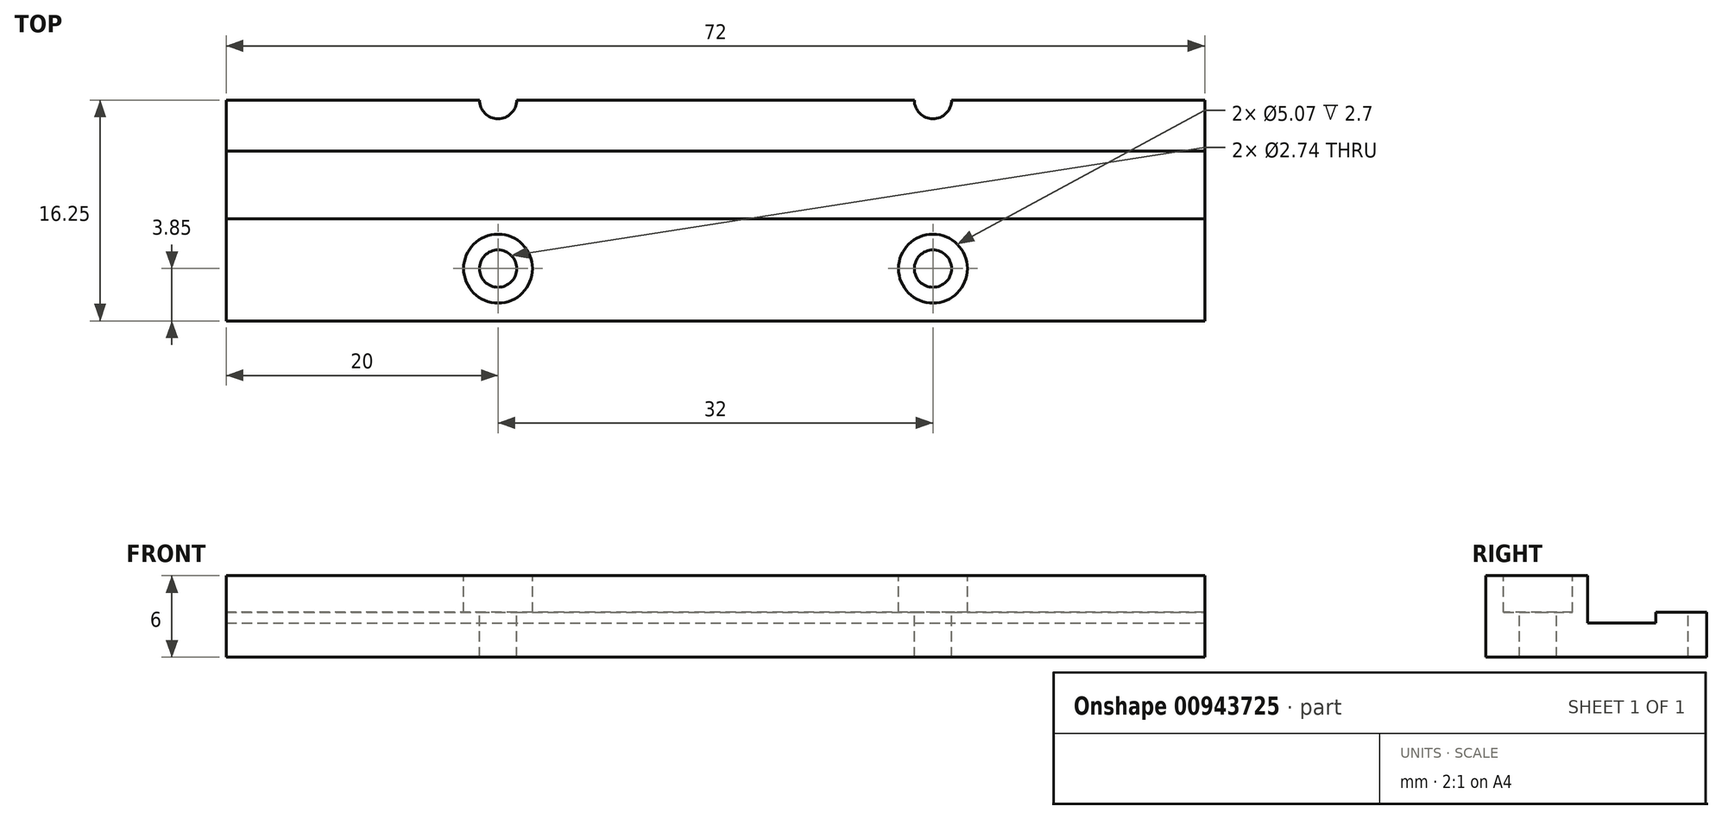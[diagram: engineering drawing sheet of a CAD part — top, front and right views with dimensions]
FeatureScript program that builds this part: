
annotation { "Feature Type Name" : "Feature", "Feature Type Description" : "" }
export const myFeature = defineFeature(function(context is Context, id is Id, definition is map)
    precondition{}
    {
        {
            var Q0;
            Q0=qCreatedBy(makeId("Top.planeOp"),FACE);
            var sketch = newSketch(context, id + "F0", { "sketchPlane" : qUnion([Q0])});
            skLineSegment(sketch, "E0.bottom", {"start": v(36, 10) * mm, "end": v(-36, 10) * mm});
            skLineSegment(sketch, "E0.top", {"start": v(36, -10) * mm, "end": v(-36, -10) * mm});
            skLineSegment(sketch, "E0.left", {"start": v(36, 10) * mm, "end": v(36, -10) * mm});
            skLineSegment(sketch, "E0.right", {"start": v(-36, 10) * mm, "end": v(-36, -10) * mm});
            skPoint(sketch, "E0.middle", {"position": v(0, 0) * mm});
            skSolve(sketch);
        }
        {
            var Q0;
            Q0=qSketchRegion(id+"F0",true);
            extrude(context, id + "F1", {"entities" : qUnion([Q0]), "depth" : 6 * mm, "offsetDistance" : 25 * mm});
        }
        {
            var Q0;
            Q0=makeQuery(id+"F1.opExtrude","SWEPT_FACE",FACE,{"disambiguationData":[OSD([sQuery(id+"F0.wireOp",EDGE,"E0.left")])]});
            var sketch = newSketch(context, id + "F2", { "sketchPlane" : qUnion([Q0])});
            skLineSegment(sketch, "E1.bottom", {"start": v(2.5, 2.5) * mm, "end": v(-2.5, 2.5) * mm});
            skLineSegment(sketch, "E1.top", {"start": v(2.5, 9.5) * mm, "end": v(-2.5, 9.5) * mm});
            skLineSegment(sketch, "E1.left", {"start": v(2.5, 2.5) * mm, "end": v(2.5, 9.5) * mm});
            skLineSegment(sketch, "E1.right", {"start": v(-2.5, 2.5) * mm, "end": v(-2.5, 9.5) * mm});
            skPoint(sketch, "E1.middle", {"position": v(0, 6) * mm});
            skSolve(sketch);
        }
        {
            var Q0;
            Q0=qSketchRegion(id+"F2",true);
            extrude(context, id + "F3", {"entities" : qUnion([Q0]), "operationType" : NewBodyOperationType.REMOVE, "oppositeDirection" : true, "depth" : 100 * mm, "offsetDistance" : 25 * mm});
        }
        {
            var Q0;
            {var subQ0=sQuery(id+"F0.wireOp",EDGE,"E0.bottom");var subQ1=sQuery(id+"F0.wireOp",EDGE,"E0.right");var subQ2=sQuery(id+"F0.wireOp",EDGE,"E0.left");Q0=makeQuery(id+"F3.boolean.opBoolean","SPLIT",FACE,{"disambiguationData":[TD([makeQuery(id+"F1.opExtrude","SWEPT_FACE",FACE,{"disambiguationData":[OSD([subQ0])]})])],"derivedFrom":makeQuery(id+"F1.opExtrude","CAP_FACE",FACE,{"disambiguationData":[OSD([subQ0,sQuery(id+"F0.wireOp",EDGE,"E0.top"),subQ2,subQ1])],"isStart":false})});}
            var sketch = newSketch(context, id + "F4", { "sketchPlane" : qUnion([Q0])});
            skLineSegment(sketch, "E2", {"start": v(-16, 10) * mm, "end": v(-16, -10) * mm});
            skLineSegment(sketch, "E3", {"start": v(16, 10) * mm, "end": v(16, -10) * mm});
            skLineSegment(sketch, "E4", {"start": v(-35.89, 0) * mm, "end": v(36.29, 0) * mm});
            skLineSegment(sketch, "E5", {"start": v(-36, 6.25) * mm, "end": v(36, 6.25) * mm});
            skLineSegment(sketch, "E6", {"start": v(-35.92, -6.15) * mm, "end": v(36.06, -6.15) * mm});
            skCircle(sketch, "E7", {"center": v(-16, -6.15) * mm, "radius": 1.37 * mm});
            skCircle(sketch, "E8", {"center": v(16, -6.15) * mm, "radius": 1.37 * mm});
            skCircle(sketch, "E9", {"center": v(16, 6.25) * mm, "radius": 1.37 * mm});
            skCircle(sketch, "E10", {"center": v(-16, 6.25) * mm, "radius": 1.37 * mm});
            skCircle(sketch, "E11", {"center": v(-16, 6.25) * mm, "radius": 2.54 * mm});
            skCircle(sketch, "E12", {"center": v(-16, -6.15) * mm, "radius": 2.54 * mm});
            skCircle(sketch, "E13", {"center": v(16, -6.15) * mm, "radius": 2.54 * mm});
            skCircle(sketch, "E14", {"center": v(16, 6.25) * mm, "radius": 2.54 * mm});
            skSolve(sketch);
        }
        {
            var Q0;
            {var subQ0=sQuery(id+"F4.wireOp",EDGE,"E11");var subQ1=sQuery(id+"F4.wireOp",EDGE,"E2");var subQ2=makeQuery(id+"F4.imprint","INTERSECT",VERTEX,{"disambiguationData":[OD(0.0)],"derivedFrom":[subQ1,subQ0]});Q0=makeQuery(id+"F4.imprint","IMPRINT",FACE,{"disambiguationData":[TD([[makeQuery(id+"F4.imprint","IMPRINT",EDGE,{"disambiguationData":[TD([[subQ2,-1.0]])],"derivedFrom":subQ1}),-1.0]])]});}
            var Q1;
            {var subQ0=sQuery(id+"F4.wireOp",EDGE,"E10");var subQ1=sQuery(id+"F4.wireOp",EDGE,"E2");var subQ2=makeQuery(id+"F4.imprint","INTERSECT",VERTEX,{"disambiguationData":[OD(1.0)],"derivedFrom":[subQ1,subQ0]});Q1=makeQuery(id+"F4.imprint","IMPRINT",FACE,{"disambiguationData":[TD([[makeQuery(id+"F4.imprint","IMPRINT",EDGE,{"disambiguationData":[TD([[subQ2,-1.0]])],"derivedFrom":subQ1}),-1.0]])]});}
            var Q2;
            {var subQ0=sQuery(id+"F4.wireOp",EDGE,"E10");var subQ1=sQuery(id+"F4.wireOp",EDGE,"E2");var subQ2=makeQuery(id+"F4.imprint","INTERSECT",VERTEX,{"disambiguationData":[OD(1.0)],"derivedFrom":[subQ1,subQ0]});Q2=makeQuery(id+"F4.imprint","IMPRINT",FACE,{"disambiguationData":[TD([[makeQuery(id+"F4.imprint","IMPRINT",EDGE,{"disambiguationData":[TD([[subQ2,-1.0]])],"derivedFrom":subQ1}),1.0]])]});}
            var Q3;
            {var subQ0=sQuery(id+"F4.wireOp",EDGE,"E11");var subQ1=sQuery(id+"F4.wireOp",EDGE,"E2");var subQ2=makeQuery(id+"F4.imprint","INTERSECT",VERTEX,{"disambiguationData":[OD(0.0)],"derivedFrom":[subQ1,subQ0]});Q3=makeQuery(id+"F4.imprint","IMPRINT",FACE,{"disambiguationData":[TD([[makeQuery(id+"F4.imprint","IMPRINT",EDGE,{"disambiguationData":[TD([[subQ2,-1.0]])],"derivedFrom":subQ1}),1.0]])]});}
            var Q4;
            {var subQ0=sQuery(id+"F4.wireOp",EDGE,"E12");var subQ1=sQuery(id+"F4.wireOp",EDGE,"E2");var subQ2=makeQuery(id+"F4.imprint","INTERSECT",VERTEX,{"disambiguationData":[OD(1.0)],"derivedFrom":[subQ1,subQ0]});Q4=makeQuery(id+"F4.imprint","IMPRINT",FACE,{"disambiguationData":[TD([[makeQuery(id+"F4.imprint","IMPRINT",EDGE,{"disambiguationData":[TD([[subQ2,-1.0]])],"derivedFrom":subQ1}),-1.0]])]});}
            var Q5;
            {var subQ0=sQuery(id+"F4.wireOp",EDGE,"E12");var subQ1=sQuery(id+"F4.wireOp",EDGE,"E2");var subQ2=makeQuery(id+"F4.imprint","INTERSECT",VERTEX,{"disambiguationData":[OD(0.0)],"derivedFrom":[subQ1,subQ0]});Q5=makeQuery(id+"F4.imprint","IMPRINT",FACE,{"disambiguationData":[TD([[makeQuery(id+"F4.imprint","IMPRINT",EDGE,{"disambiguationData":[TD([[subQ2,1.0]])],"derivedFrom":subQ1}),-1.0]])]});}
            var Q6;
            {var subQ0=sQuery(id+"F4.wireOp",EDGE,"E12");var subQ1=sQuery(id+"F4.wireOp",EDGE,"E2");var subQ2=makeQuery(id+"F4.imprint","INTERSECT",VERTEX,{"disambiguationData":[OD(0.0)],"derivedFrom":[subQ1,subQ0]});Q6=makeQuery(id+"F4.imprint","IMPRINT",FACE,{"disambiguationData":[TD([[makeQuery(id+"F4.imprint","IMPRINT",EDGE,{"disambiguationData":[TD([[subQ2,1.0]])],"derivedFrom":subQ1}),1.0]])]});}
            var Q7;
            {var subQ0=sQuery(id+"F4.wireOp",EDGE,"E12");var subQ1=sQuery(id+"F4.wireOp",EDGE,"E2");var subQ2=makeQuery(id+"F4.imprint","INTERSECT",VERTEX,{"disambiguationData":[OD(1.0)],"derivedFrom":[subQ1,subQ0]});Q7=makeQuery(id+"F4.imprint","IMPRINT",FACE,{"disambiguationData":[TD([[makeQuery(id+"F4.imprint","IMPRINT",EDGE,{"disambiguationData":[TD([[subQ2,-1.0]])],"derivedFrom":subQ1}),1.0]])]});}
            var Q8;
            {var subQ0=sQuery(id+"F4.wireOp",EDGE,"E13");var subQ1=sQuery(id+"F4.wireOp",EDGE,"E3");var subQ2=makeQuery(id+"F4.imprint","INTERSECT",VERTEX,{"disambiguationData":[OD(0.0)],"derivedFrom":[subQ1,subQ0]});Q8=makeQuery(id+"F4.imprint","IMPRINT",FACE,{"disambiguationData":[TD([[makeQuery(id+"F4.imprint","IMPRINT",EDGE,{"disambiguationData":[TD([[subQ2,1.0]])],"derivedFrom":subQ1}),-1.0]])]});}
            var Q9;
            {var subQ0=sQuery(id+"F4.wireOp",EDGE,"E13");var subQ1=sQuery(id+"F4.wireOp",EDGE,"E3");var subQ2=makeQuery(id+"F4.imprint","INTERSECT",VERTEX,{"disambiguationData":[OD(1.0)],"derivedFrom":[subQ1,subQ0]});Q9=makeQuery(id+"F4.imprint","IMPRINT",FACE,{"disambiguationData":[TD([[makeQuery(id+"F4.imprint","IMPRINT",EDGE,{"disambiguationData":[TD([[subQ2,-1.0]])],"derivedFrom":subQ1}),-1.0]])]});}
            var Q10;
            {var subQ0=sQuery(id+"F4.wireOp",EDGE,"E13");var subQ1=sQuery(id+"F4.wireOp",EDGE,"E3");var subQ2=makeQuery(id+"F4.imprint","INTERSECT",VERTEX,{"disambiguationData":[OD(1.0)],"derivedFrom":[subQ1,subQ0]});Q10=makeQuery(id+"F4.imprint","IMPRINT",FACE,{"disambiguationData":[TD([[makeQuery(id+"F4.imprint","IMPRINT",EDGE,{"disambiguationData":[TD([[subQ2,-1.0]])],"derivedFrom":subQ1}),1.0]])]});}
            var Q11;
            {var subQ0=sQuery(id+"F4.wireOp",EDGE,"E13");var subQ1=sQuery(id+"F4.wireOp",EDGE,"E3");var subQ2=makeQuery(id+"F4.imprint","INTERSECT",VERTEX,{"disambiguationData":[OD(0.0)],"derivedFrom":[subQ1,subQ0]});Q11=makeQuery(id+"F4.imprint","IMPRINT",FACE,{"disambiguationData":[TD([[makeQuery(id+"F4.imprint","IMPRINT",EDGE,{"disambiguationData":[TD([[subQ2,1.0]])],"derivedFrom":subQ1}),1.0]])]});}
            var Q12;
            {var subQ0=sQuery(id+"F4.wireOp",EDGE,"E9");var subQ1=sQuery(id+"F4.wireOp",EDGE,"E3");var subQ2=makeQuery(id+"F4.imprint","INTERSECT",VERTEX,{"disambiguationData":[OD(1.0)],"derivedFrom":[subQ1,subQ0]});Q12=makeQuery(id+"F4.imprint","IMPRINT",FACE,{"disambiguationData":[TD([[makeQuery(id+"F4.imprint","IMPRINT",EDGE,{"disambiguationData":[TD([[subQ2,-1.0]])],"derivedFrom":subQ1}),-1.0]])]});}
            var Q13;
            {var subQ0=sQuery(id+"F4.wireOp",EDGE,"E14");var subQ1=sQuery(id+"F4.wireOp",EDGE,"E3");var subQ2=makeQuery(id+"F4.imprint","INTERSECT",VERTEX,{"disambiguationData":[OD(0.0)],"derivedFrom":[subQ1,subQ0]});Q13=makeQuery(id+"F4.imprint","IMPRINT",FACE,{"disambiguationData":[TD([[makeQuery(id+"F4.imprint","IMPRINT",EDGE,{"disambiguationData":[TD([[subQ2,-1.0]])],"derivedFrom":subQ1}),-1.0]])]});}
            var Q14;
            {var subQ0=sQuery(id+"F4.wireOp",EDGE,"E14");var subQ1=sQuery(id+"F4.wireOp",EDGE,"E3");var subQ2=makeQuery(id+"F4.imprint","INTERSECT",VERTEX,{"disambiguationData":[OD(0.0)],"derivedFrom":[subQ1,subQ0]});Q14=makeQuery(id+"F4.imprint","IMPRINT",FACE,{"disambiguationData":[TD([[makeQuery(id+"F4.imprint","IMPRINT",EDGE,{"disambiguationData":[TD([[subQ2,-1.0]])],"derivedFrom":subQ1}),1.0]])]});}
            var Q15;
            {var subQ0=sQuery(id+"F4.wireOp",EDGE,"E9");var subQ1=sQuery(id+"F4.wireOp",EDGE,"E3");var subQ2=makeQuery(id+"F4.imprint","INTERSECT",VERTEX,{"disambiguationData":[OD(1.0)],"derivedFrom":[subQ1,subQ0]});Q15=makeQuery(id+"F4.imprint","IMPRINT",FACE,{"disambiguationData":[TD([[makeQuery(id+"F4.imprint","IMPRINT",EDGE,{"disambiguationData":[TD([[subQ2,-1.0]])],"derivedFrom":subQ1}),1.0]])]});}
            extrude(context, id + "F5", {"entities" : qUnion([Q0, Q1, Q2, Q3, Q4, Q5, Q6, Q7, Q8, Q9, Q10, Q11, Q12, Q13, Q14, Q15]), "operationType" : NewBodyOperationType.REMOVE, "oppositeDirection" : true, "depth" : 2.7 * mm, "offsetDistance" : 25 * mm});
        }
        {
            var Q0;
            {var subQ0=sQuery(id+"F0.wireOp",EDGE,"E0.bottom");var subQ1=sQuery(id+"F0.wireOp",EDGE,"E0.right");var subQ2=sQuery(id+"F0.wireOp",EDGE,"E0.left");Q0=makeQuery(id+"F5.boolean.opBoolean","SPLIT",FACE,{"disambiguationData":[TD([makeQuery(id+"F5.opExtrude","SWEPT_FACE",FACE,{"disambiguationData":[OSD([sQuery(id+"F4.wireOp",EDGE,"E10")])]})])],"derivedFrom":makeQuery(id+"F3.boolean.opBoolean","SPLIT",FACE,{"disambiguationData":[TD([makeQuery(id+"F1.opExtrude","SWEPT_FACE",FACE,{"disambiguationData":[OSD([subQ0])]})])],"derivedFrom":makeQuery(id+"F1.opExtrude","CAP_FACE",FACE,{"disambiguationData":[OSD([subQ0,sQuery(id+"F0.wireOp",EDGE,"E0.top"),subQ2,subQ1])],"isStart":false})})});}
            var Q1;
            {var subQ0=sQuery(id+"F0.wireOp",EDGE,"E0.top");var subQ1=sQuery(id+"F0.wireOp",EDGE,"E0.left");var subQ2=sQuery(id+"F0.wireOp",EDGE,"E0.right");Q1=makeQuery(id+"F5.boolean.opBoolean","SPLIT",FACE,{"disambiguationData":[TD([makeQuery(id+"F5.opExtrude","SWEPT_FACE",FACE,{"disambiguationData":[OSD([sQuery(id+"F4.wireOp",EDGE,"E7")])]})])],"derivedFrom":makeQuery(id+"F3.boolean.opBoolean","SPLIT",FACE,{"disambiguationData":[TD([makeQuery(id+"F1.opExtrude","SWEPT_FACE",FACE,{"disambiguationData":[OSD([subQ0])]})])],"derivedFrom":makeQuery(id+"F1.opExtrude","CAP_FACE",FACE,{"disambiguationData":[OSD([sQuery(id+"F0.wireOp",EDGE,"E0.bottom"),subQ0,subQ1,subQ2])],"isStart":false})})});}
            var Q2;
            {var subQ0=sQuery(id+"F0.wireOp",EDGE,"E0.top");var subQ1=sQuery(id+"F0.wireOp",EDGE,"E0.left");var subQ2=sQuery(id+"F0.wireOp",EDGE,"E0.right");Q2=makeQuery(id+"F5.boolean.opBoolean","SPLIT",FACE,{"disambiguationData":[TD([makeQuery(id+"F5.opExtrude","SWEPT_FACE",FACE,{"disambiguationData":[OSD([sQuery(id+"F4.wireOp",EDGE,"E8")])]})])],"derivedFrom":makeQuery(id+"F3.boolean.opBoolean","SPLIT",FACE,{"disambiguationData":[TD([makeQuery(id+"F1.opExtrude","SWEPT_FACE",FACE,{"disambiguationData":[OSD([subQ0])]})])],"derivedFrom":makeQuery(id+"F1.opExtrude","CAP_FACE",FACE,{"disambiguationData":[OSD([sQuery(id+"F0.wireOp",EDGE,"E0.bottom"),subQ0,subQ1,subQ2])],"isStart":false})})});}
            var Q3;
            {var subQ0=sQuery(id+"F0.wireOp",EDGE,"E0.bottom");var subQ1=sQuery(id+"F0.wireOp",EDGE,"E0.right");var subQ2=sQuery(id+"F0.wireOp",EDGE,"E0.left");Q3=makeQuery(id+"F5.boolean.opBoolean","SPLIT",FACE,{"disambiguationData":[TD([makeQuery(id+"F5.opExtrude","SWEPT_FACE",FACE,{"disambiguationData":[OSD([sQuery(id+"F4.wireOp",EDGE,"E9")])]})])],"derivedFrom":makeQuery(id+"F3.boolean.opBoolean","SPLIT",FACE,{"disambiguationData":[TD([makeQuery(id+"F1.opExtrude","SWEPT_FACE",FACE,{"disambiguationData":[OSD([subQ0])]})])],"derivedFrom":makeQuery(id+"F1.opExtrude","CAP_FACE",FACE,{"disambiguationData":[OSD([subQ0,sQuery(id+"F0.wireOp",EDGE,"E0.top"),subQ2,subQ1])],"isStart":false})})});}
            extrude(context, id + "F6", {"entities" : qUnion([Q0, Q1, Q2, Q3]), "operationType" : NewBodyOperationType.REMOVE, "oppositeDirection" : true, "depth" : 25 * mm, "offsetDistance" : 25 * mm});
        }
    });
